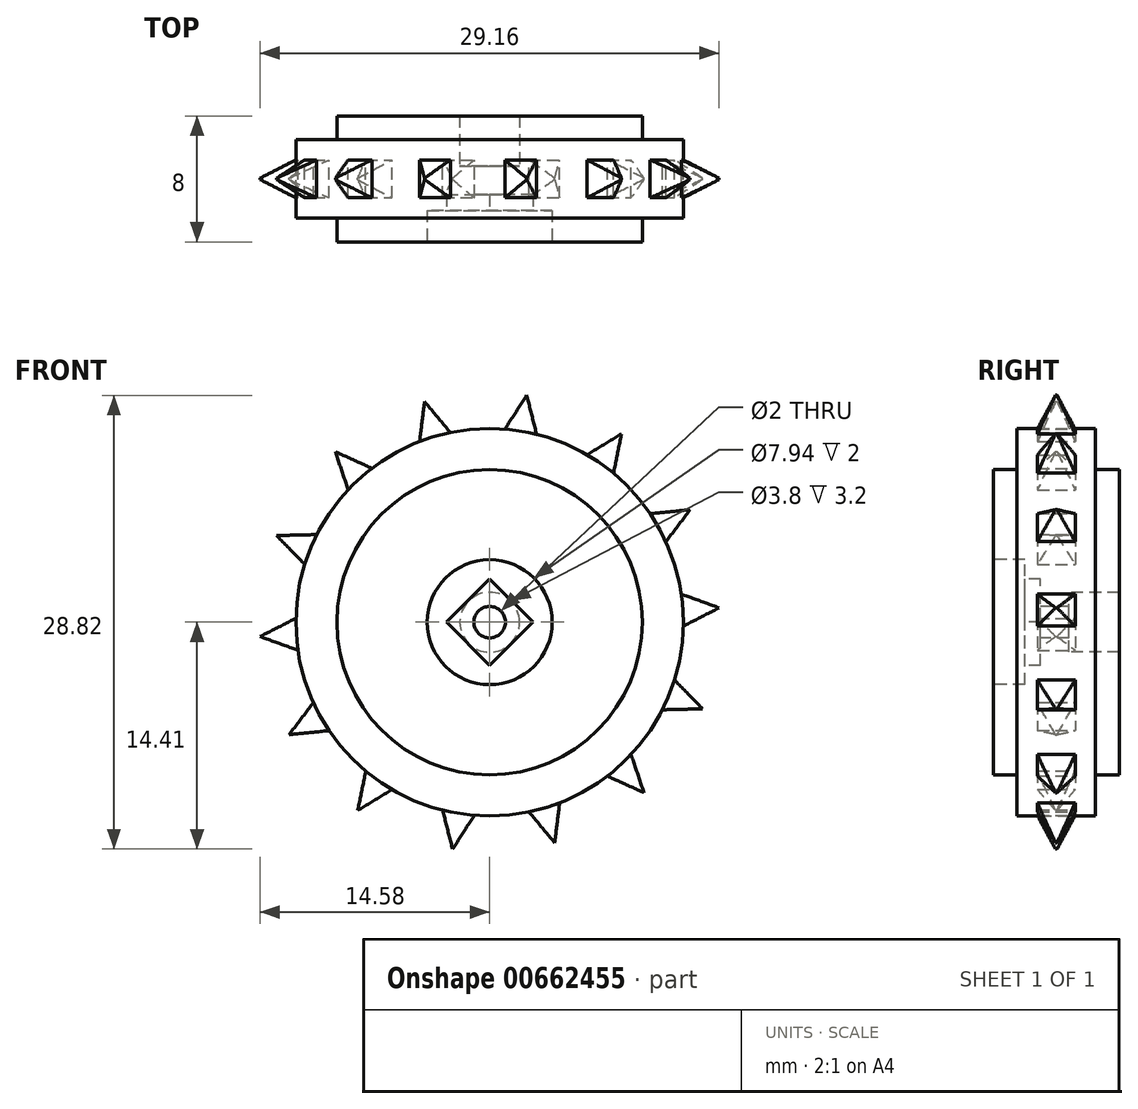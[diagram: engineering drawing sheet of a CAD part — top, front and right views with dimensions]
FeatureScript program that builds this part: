
annotation { "Feature Type Name" : "Feature", "Feature Type Description" : "" }
export const myFeature = defineFeature(function(context is Context, id is Id, definition is map)
    precondition{}
    {
        {
            var Q0;
            Q0=qCreatedBy(makeId("Front.planeOp"),FACE);
            var sketch = newSketch(context, id + "F0", { "sketchPlane" : qUnion([Q0])});
            skCircle(sketch, "E0.cCircle", {"center": v(-22.86, 35.79) * mm, "radius": 14.24 * mm, "construction": true});
            skLineSegment(sketch, "E0.0", {"start": v(-9.33, 30.29) * mm, "end": v(-13.06, 24.96) * mm});
            skLineSegment(sketch, "E0.1", {"start": v(-13.06, 24.96) * mm, "end": v(-18.73, 21.78) * mm});
            skLineSegment(sketch, "E0.2", {"start": v(-18.73, 21.78) * mm, "end": v(-25.21, 21.38) * mm});
            skLineSegment(sketch, "E0.3", {"start": v(-25.21, 21.38) * mm, "end": v(-31.24, 23.82) * mm});
            skLineSegment(sketch, "E0.4", {"start": v(-31.24, 23.82) * mm, "end": v(-35.6, 28.64) * mm});
            skLineSegment(sketch, "E0.5", {"start": v(-35.6, 28.64) * mm, "end": v(-37.44, 34.88) * mm});
            skLineSegment(sketch, "E0.6", {"start": v(-37.44, 34.88) * mm, "end": v(-36.39, 41.3) * mm});
            skLineSegment(sketch, "E0.7", {"start": v(-36.39, 41.3) * mm, "end": v(-32.66, 46.62) * mm});
            skLineSegment(sketch, "E0.8", {"start": v(-32.66, 46.62) * mm, "end": v(-27, 49.8) * mm});
            skLineSegment(sketch, "E0.9", {"start": v(-27, 49.8) * mm, "end": v(-20.5, 50.2) * mm});
            skLineSegment(sketch, "E0.10", {"start": v(-20.5, 50.2) * mm, "end": v(-14.48, 47.75) * mm});
            skLineSegment(sketch, "E0.11", {"start": v(-14.48, 47.75) * mm, "end": v(-10.12, 42.94) * mm});
            skLineSegment(sketch, "E0.12", {"start": v(-10.12, 42.94) * mm, "end": v(-8.28, 36.7) * mm});
            skLineSegment(sketch, "E0.13", {"start": v(-8.28, 36.7) * mm, "end": v(-9.33, 30.29) * mm});
            skPoint(sketch, "E0.0.midPoint", {"position": v(-11.2, 27.62) * mm});
            skLineSegment(sketch, "E1", {"start": v(-27, 49.8) * mm, "end": v(-22.86, 35.79) * mm});
            skLineSegment(sketch, "E2", {"start": v(-27, 49.8) * mm, "end": v(-27.37, 46.77) * mm});
            skLineSegment(sketch, "E3", {"start": v(-27.37, 46.77) * mm, "end": v(-26.2, 47.11) * mm, "construction": true});
            skLineSegment(sketch, "E4.MirrorCS", {"start": v(-27, 49.8) * mm, "end": v(-25.03, 47.46) * mm});
            skPoint(sketch, "E5", {"position": v(-26.34, 47.6) * mm});
            skPoint(sketch, "E6", {"position": v(-25.6, 45.1) * mm});
            skCircle(sketch, "E7", {"center": v(-22.86, 35.79) * mm, "radius": 9.7 * mm});
            skCircle(sketch, "E8", {"center": v(-22.86, 35.79) * mm, "radius": 12.3 * mm});
            skLineSegment(sketch, "E9.1.0", {"start": v(-32.66, 46.62) * mm, "end": v(-31.69, 43.72) * mm});
            skLineSegment(sketch, "E9.1.1", {"start": v(-32.66, 46.62) * mm, "end": v(-29.88, 45.36) * mm});
            skLineSegment(sketch, "E9.2.0", {"start": v(-36.39, 41.3) * mm, "end": v(-34.25, 39.1) * mm});
            skLineSegment(sketch, "E9.2.1", {"start": v(-36.39, 41.3) * mm, "end": v(-33.34, 41.37) * mm});
            skLineSegment(sketch, "E9.3.0", {"start": v(-37.44, 34.88) * mm, "end": v(-34.57, 33.84) * mm});
            skLineSegment(sketch, "E9.3.1", {"start": v(-37.44, 34.88) * mm, "end": v(-34.72, 36.27) * mm});
            skLineSegment(sketch, "E9.4.0", {"start": v(-35.6, 28.64) * mm, "end": v(-32.56, 28.95) * mm});
            skLineSegment(sketch, "E9.4.1", {"start": v(-35.6, 28.64) * mm, "end": v(-33.75, 31.08) * mm});
            skLineSegment(sketch, "E9.5.0", {"start": v(-31.24, 23.82) * mm, "end": v(-28.63, 25.42) * mm});
            skLineSegment(sketch, "E9.5.1", {"start": v(-31.24, 23.82) * mm, "end": v(-30.63, 26.82) * mm});
            skLineSegment(sketch, "E9.6.0", {"start": v(-25.21, 21.38) * mm, "end": v(-23.56, 23.94) * mm});
            skLineSegment(sketch, "E9.6.1", {"start": v(-25.21, 21.38) * mm, "end": v(-25.97, 24.34) * mm});
            skLineSegment(sketch, "E9.7.0", {"start": v(-18.73, 21.78) * mm, "end": v(-18.35, 24.81) * mm});
            skLineSegment(sketch, "E9.7.1", {"start": v(-18.73, 21.78) * mm, "end": v(-20.69, 24.12) * mm});
            skLineSegment(sketch, "E9.8.0", {"start": v(-13.06, 24.96) * mm, "end": v(-14.04, 27.85) * mm});
            skLineSegment(sketch, "E9.8.1", {"start": v(-13.06, 24.96) * mm, "end": v(-15.84, 26.22) * mm});
            skLineSegment(sketch, "E9.9.0", {"start": v(-9.33, 30.29) * mm, "end": v(-11.47, 32.47) * mm});
            skLineSegment(sketch, "E9.9.1", {"start": v(-9.33, 30.29) * mm, "end": v(-12.38, 30.21) * mm});
            skLineSegment(sketch, "E9.10.0", {"start": v(-8.28, 36.7) * mm, "end": v(-11.15, 37.74) * mm});
            skLineSegment(sketch, "E9.10.1", {"start": v(-8.28, 36.7) * mm, "end": v(-11, 35.31) * mm});
            skLineSegment(sketch, "E9.11.0", {"start": v(-10.12, 42.94) * mm, "end": v(-13.16, 42.63) * mm});
            skLineSegment(sketch, "E9.11.1", {"start": v(-10.12, 42.94) * mm, "end": v(-11.97, 40.5) * mm});
            skLineSegment(sketch, "E9.12.0", {"start": v(-14.48, 47.75) * mm, "end": v(-17.09, 46.16) * mm});
            skLineSegment(sketch, "E9.12.1", {"start": v(-14.48, 47.75) * mm, "end": v(-15.1, 44.76) * mm});
            skLineSegment(sketch, "E9.13.0", {"start": v(-20.5, 50.2) * mm, "end": v(-22.16, 47.64) * mm});
            skLineSegment(sketch, "E9.13.1", {"start": v(-20.5, 50.2) * mm, "end": v(-19.76, 47.24) * mm});
            skSolve(sketch);
        }
        {
            var Q0;
            Q0=makeQuery(id+"F0.imprint","IMPRINT",FACE,{"disambiguationData":[TD([[makeQuery(id+"F0.imprint","IMPRINT",EDGE,{"derivedFrom":sQuery(id+"F0.wireOp",EDGE,"E7")}),-1.0]])]});
            var Q1;
            {var subQ0=sQuery(id+"F0.wireOp",EDGE,"E9.2.1");var subQ1=sQuery(id+"F0.wireOp",EDGE,"E8");var subQ2=makeQuery(id+"F0.imprint","INTERSECT",VERTEX,{"derivedFrom":[subQ1,subQ0]});Q1=makeQuery(id+"F0.imprint","IMPRINT",FACE,{"disambiguationData":[TD([[makeQuery(id+"F0.imprint","IMPRINT",EDGE,{"disambiguationData":[TD([[subQ2,-1.0]])],"derivedFrom":subQ1}),-1.0]])]});}
            var Q2;
            {var subQ1=sQuery(id+"F0.wireOp",EDGE,"E2");var subQ3=sQuery(id+"F0.wireOp",EDGE,"E8");var subQ4=makeQuery(id+"F0.imprint","INTERSECT",VERTEX,{"derivedFrom":[subQ1,subQ3]});Q2=makeQuery(id+"F0.imprint","IMPRINT",FACE,{"disambiguationData":[TD([[makeQuery(id+"F0.imprint","IMPRINT",EDGE,{"disambiguationData":[TD([[subQ4,1.0]])],"derivedFrom":subQ3}),-1.0]])]});}
            var Q3;
            {var subQ0=sQuery(id+"F0.wireOp",EDGE,"E9.13.1");var subQ1=sQuery(id+"F0.wireOp",EDGE,"E8");var subQ2=makeQuery(id+"F0.imprint","INTERSECT",VERTEX,{"derivedFrom":[subQ1,subQ0]});Q3=makeQuery(id+"F0.imprint","IMPRINT",FACE,{"disambiguationData":[TD([[makeQuery(id+"F0.imprint","IMPRINT",EDGE,{"disambiguationData":[TD([[subQ2,-1.0]])],"derivedFrom":subQ1}),-1.0]])]});}
            var Q4;
            {var subQ0=sQuery(id+"F0.wireOp",EDGE,"E9.12.1");var subQ1=sQuery(id+"F0.wireOp",EDGE,"E8");var subQ2=makeQuery(id+"F0.imprint","INTERSECT",VERTEX,{"derivedFrom":[subQ1,subQ0]});Q4=makeQuery(id+"F0.imprint","IMPRINT",FACE,{"disambiguationData":[TD([[makeQuery(id+"F0.imprint","IMPRINT",EDGE,{"disambiguationData":[TD([[subQ2,-1.0]])],"derivedFrom":subQ1}),-1.0]])]});}
            var Q5;
            {var subQ0=sQuery(id+"F0.wireOp",EDGE,"E9.11.1");var subQ1=sQuery(id+"F0.wireOp",EDGE,"E8");var subQ2=makeQuery(id+"F0.imprint","INTERSECT",VERTEX,{"derivedFrom":[subQ1,subQ0]});Q5=makeQuery(id+"F0.imprint","IMPRINT",FACE,{"disambiguationData":[TD([[makeQuery(id+"F0.imprint","IMPRINT",EDGE,{"disambiguationData":[TD([[subQ2,-1.0]])],"derivedFrom":subQ1}),-1.0]])]});}
            var Q6;
            {var subQ0=sQuery(id+"F0.wireOp",EDGE,"E9.10.0");var subQ1=sQuery(id+"F0.wireOp",EDGE,"E8");var subQ2=makeQuery(id+"F0.imprint","INTERSECT",VERTEX,{"derivedFrom":[subQ1,subQ0]});Q6=makeQuery(id+"F0.imprint","IMPRINT",FACE,{"disambiguationData":[TD([[makeQuery(id+"F0.imprint","IMPRINT",EDGE,{"disambiguationData":[TD([[subQ2,1.0]])],"derivedFrom":subQ1}),-1.0]])]});}
            var Q7;
            {var subQ0=sQuery(id+"F0.wireOp",EDGE,"E9.9.1");var subQ1=sQuery(id+"F0.wireOp",EDGE,"E8");var subQ2=makeQuery(id+"F0.imprint","INTERSECT",VERTEX,{"derivedFrom":[subQ1,subQ0]});Q7=makeQuery(id+"F0.imprint","IMPRINT",FACE,{"disambiguationData":[TD([[makeQuery(id+"F0.imprint","IMPRINT",EDGE,{"disambiguationData":[TD([[subQ2,-1.0]])],"derivedFrom":subQ1}),-1.0]])]});}
            var Q8;
            {var subQ0=sQuery(id+"F0.wireOp",EDGE,"E9.8.1");var subQ1=sQuery(id+"F0.wireOp",EDGE,"E8");var subQ2=makeQuery(id+"F0.imprint","INTERSECT",VERTEX,{"derivedFrom":[subQ1,subQ0]});Q8=makeQuery(id+"F0.imprint","IMPRINT",FACE,{"disambiguationData":[TD([[makeQuery(id+"F0.imprint","IMPRINT",EDGE,{"disambiguationData":[TD([[subQ2,-1.0]])],"derivedFrom":subQ1}),-1.0]])]});}
            var Q9;
            {var subQ0=sQuery(id+"F0.wireOp",EDGE,"E9.7.1");var subQ1=sQuery(id+"F0.wireOp",EDGE,"E8");var subQ2=makeQuery(id+"F0.imprint","INTERSECT",VERTEX,{"derivedFrom":[subQ1,subQ0]});Q9=makeQuery(id+"F0.imprint","IMPRINT",FACE,{"disambiguationData":[TD([[makeQuery(id+"F0.imprint","IMPRINT",EDGE,{"disambiguationData":[TD([[subQ2,-1.0]])],"derivedFrom":subQ1}),-1.0]])]});}
            var Q10;
            {var subQ0=sQuery(id+"F0.wireOp",EDGE,"E9.6.1");var subQ1=sQuery(id+"F0.wireOp",EDGE,"E8");var subQ2=makeQuery(id+"F0.imprint","INTERSECT",VERTEX,{"derivedFrom":[subQ1,subQ0]});Q10=makeQuery(id+"F0.imprint","IMPRINT",FACE,{"disambiguationData":[TD([[makeQuery(id+"F0.imprint","IMPRINT",EDGE,{"disambiguationData":[TD([[subQ2,-1.0]])],"derivedFrom":subQ1}),-1.0]])]});}
            var Q11;
            {var subQ0=sQuery(id+"F0.wireOp",EDGE,"E9.5.1");var subQ1=sQuery(id+"F0.wireOp",EDGE,"E8");var subQ2=makeQuery(id+"F0.imprint","INTERSECT",VERTEX,{"derivedFrom":[subQ1,subQ0]});Q11=makeQuery(id+"F0.imprint","IMPRINT",FACE,{"disambiguationData":[TD([[makeQuery(id+"F0.imprint","IMPRINT",EDGE,{"disambiguationData":[TD([[subQ2,-1.0]])],"derivedFrom":subQ1}),-1.0]])]});}
            var Q12;
            {var subQ0=sQuery(id+"F0.wireOp",EDGE,"E9.4.1");var subQ1=sQuery(id+"F0.wireOp",EDGE,"E8");var subQ2=makeQuery(id+"F0.imprint","INTERSECT",VERTEX,{"derivedFrom":[subQ1,subQ0]});Q12=makeQuery(id+"F0.imprint","IMPRINT",FACE,{"disambiguationData":[TD([[makeQuery(id+"F0.imprint","IMPRINT",EDGE,{"disambiguationData":[TD([[subQ2,-1.0]])],"derivedFrom":subQ1}),-1.0]])]});}
            var Q13;
            {var subQ0=sQuery(id+"F0.wireOp",EDGE,"E9.3.1");var subQ1=sQuery(id+"F0.wireOp",EDGE,"E8");var subQ2=makeQuery(id+"F0.imprint","INTERSECT",VERTEX,{"derivedFrom":[subQ1,subQ0]});Q13=makeQuery(id+"F0.imprint","IMPRINT",FACE,{"disambiguationData":[TD([[makeQuery(id+"F0.imprint","IMPRINT",EDGE,{"disambiguationData":[TD([[subQ2,-1.0]])],"derivedFrom":subQ1}),-1.0]])]});}
            var Q14;
            Q14=makeQuery(id+"F0.imprint","IMPRINT",FACE,{"disambiguationData":[TD([[makeQuery(id+"F0.imprint","IMPRINT",EDGE,{"derivedFrom":sQuery(id+"F0.wireOp",EDGE,"E7")}),1.0]])]});
            var Q15;
            {var subQ0=sQuery(id+"F0.wireOp",EDGE,"E9.1.1");var subQ1=sQuery(id+"F0.wireOp",EDGE,"E8");var subQ2=makeQuery(id+"F0.imprint","INTERSECT",VERTEX,{"derivedFrom":[subQ1,subQ0]});Q15=makeQuery(id+"F0.imprint","IMPRINT",FACE,{"disambiguationData":[TD([[makeQuery(id+"F0.imprint","IMPRINT",EDGE,{"disambiguationData":[TD([[subQ2,-1.0]])],"derivedFrom":subQ1}),-1.0]])]});}
            var Q16;
            {var subQ1=sQuery(id+"F0.wireOp",EDGE,"E1");var subQ3=sQuery(id+"F0.wireOp",EDGE,"E8");var subQ4=makeQuery(id+"F0.imprint","INTERSECT",VERTEX,{"derivedFrom":[subQ1,subQ3]});Q16=makeQuery(id+"F0.imprint","IMPRINT",FACE,{"disambiguationData":[TD([[makeQuery(id+"F0.imprint","IMPRINT",EDGE,{"disambiguationData":[TD([[subQ4,1.0]])],"derivedFrom":subQ3}),-1.0]])]});}
            extrude(context, id + "F1", {"entities" : qUnion([Q0, Q1, Q2, Q3, Q4, Q5, Q6, Q7, Q8, Q9, Q10, Q11, Q12, Q13, Q14, Q15, Q16]), "endBound" : BoundingType.SYMMETRIC, "depth" : 2.4 * mm, "offsetDistance" : 25 * mm});
        }
        {
            var Q0;
            Q0=makeQuery(id+"F0.imprint","IMPRINT",FACE,{"disambiguationData":[TD([[makeQuery(id+"F0.imprint","IMPRINT",EDGE,{"derivedFrom":sQuery(id+"F0.wireOp",EDGE,"E7")}),-1.0]])]});
            var Q1;
            Q1=makeQuery(id+"F0.imprint","IMPRINT",FACE,{"disambiguationData":[TD([[makeQuery(id+"F0.imprint","IMPRINT",EDGE,{"derivedFrom":sQuery(id+"F0.wireOp",EDGE,"E7")}),1.0]])]});
            extrude(context, id + "F2", {"entities" : qUnion([Q0, Q1]), "operationType" : NewBodyOperationType.ADD, "endBound" : BoundingType.SYMMETRIC, "depth" : 5 * mm, "offsetDistance" : 25 * mm});
        }
        {
            var Q0;
            Q0=makeQuery(id+"F0.imprint","IMPRINT",FACE,{"disambiguationData":[TD([[makeQuery(id+"F0.imprint","IMPRINT",EDGE,{"derivedFrom":sQuery(id+"F0.wireOp",EDGE,"E7")}),1.0]])]});
            extrude(context, id + "F3", {"entities" : qUnion([Q0]), "operationType" : NewBodyOperationType.ADD, "endBound" : BoundingType.SYMMETRIC, "depth" : 8 * mm, "offsetDistance" : 25 * mm});
        }
        {
            var Q0;
            Q0=makeQuery(id+"F3.opExtrude","CAP_FACE",FACE,{"disambiguationData":[OSD([sQuery(id+"F0.wireOp",EDGE,"E7")])],"isStart":false});
            var sketch = newSketch(context, id + "F4", { "sketchPlane" : qUnion([Q0])});
            skPoint(sketch, "E10.0", {"position": v(-22.86, 35.79) * mm});
            skCircle(sketch, "E11.cCircle", {"center": v(-22.86, 35.79) * mm, "radius": 2.75 * mm, "construction": true});
            skLineSegment(sketch, "E11.0", {"start": v(-25.61, 35.79) * mm, "end": v(-22.86, 38.54) * mm});
            skLineSegment(sketch, "E11.1", {"start": v(-22.86, 38.54) * mm, "end": v(-20.1, 35.79) * mm});
            skLineSegment(sketch, "E11.2", {"start": v(-20.1, 35.79) * mm, "end": v(-22.86, 33.04) * mm});
            skLineSegment(sketch, "E11.3", {"start": v(-22.86, 33.04) * mm, "end": v(-25.61, 35.79) * mm});
            skCircle(sketch, "E12", {"center": v(-22.86, 35.79) * mm, "radius": 1 * mm});
            skCircle(sketch, "E13", {"center": v(-22.86, 35.79) * mm, "radius": 3.97 * mm});
            skCircle(sketch, "E14.0", {"center": v(-22.86, 35.79) * mm, "radius": 9.7 * mm});
            skSolve(sketch);
        }
        {
            var Q0;
            Q0=makeQuery(id+"F4.imprint","IMPRINT",FACE,{"disambiguationData":[TD([[makeQuery(id+"F4.imprint","IMPRINT",EDGE,{"derivedFrom":sQuery(id+"F4.wireOp",EDGE,"E12")}),1.0]])]});
            extrude(context, id + "F5", {"entities" : qUnion([Q0]), "operationType" : NewBodyOperationType.REMOVE, "endBound" : BoundingType.THROUGH_ALL, "oppositeDirection" : true, "depth" : 25 * mm, "offsetDistance" : 25 * mm});
        }
        {
            var Q0;
            Q0=makeQuery(id+"F4.imprint","IMPRINT",FACE,{"disambiguationData":[TD([[makeQuery(id+"F4.imprint","IMPRINT",EDGE,{"derivedFrom":sQuery(id+"F4.wireOp",EDGE,"E11.0")}),-1.0]])]});
            extrude(context, id + "F6", {"entities" : qUnion([Q0]), "operationType" : NewBodyOperationType.REMOVE, "oppositeDirection" : true, "depth" : 3 * mm, "offsetDistance" : 25 * mm});
        }
        {
            var Q0;
            Q0=makeQuery(id+"F4.imprint","IMPRINT",FACE,{"disambiguationData":[TD([[makeQuery(id+"F4.imprint","IMPRINT",EDGE,{"derivedFrom":sQuery(id+"F4.wireOp",EDGE,"E11.0")}),1.0]])]});
            extrude(context, id + "F7", {"entities" : qUnion([Q0]), "operationType" : NewBodyOperationType.REMOVE, "oppositeDirection" : true, "depth" : 2 * mm, "offsetDistance" : 25 * mm});
        }
        {
            var Q0;
            Q0=sQuery(id+"F0.wireOp",EDGE,"E1");
            extrude(context, id + "F8", {"bodyType" : ToolBodyType.SURFACE, "surfaceEntities" : qUnion([Q0]), "endBound" : BoundingType.SYMMETRIC, "depth" : 6 * mm, "offsetDistance" : 25 * mm});
        }
        {
            var Q0;
            Q0=makeQuery(id+"F8.opExtrude","SWEPT_FACE",FACE,{"disambiguationData":[OSD([sQuery(id+"F0.wireOp",EDGE,"E1")])]});
            var sketch = newSketch(context, id + "F9", { "sketchPlane" : qUnion([Q0])});
            skPoint(sketch, "E15.0", {"position": v(0, 55.4) * mm});
            skLineSegment(sketch, "E16.0", {"start": v(-1.2, 55.4) * mm, "end": v(-1.2, 53.06) * mm});
            skLineSegment(sketch, "E16.1", {"start": v(1.2, 55.4) * mm, "end": v(1.2, 53.06) * mm});
            skPoint(sketch, "E16.2", {"position": v(1.2, 53.1) * mm});
            skPoint(sketch, "E16.3", {"position": v(-1.2, 53.1) * mm});
            skLineSegment(sketch, "E17", {"start": v(-1.2, 53.1) * mm, "end": v(-0.04, 55.4) * mm});
            skLineSegment(sketch, "E18", {"start": v(-0.04, 55.4) * mm, "end": v(-1.2, 55.4) * mm});
            skLineSegment(sketch, "E19", {"start": v(0, 55.4) * mm, "end": v(0, 52.96) * mm, "construction": true});
            skLineSegment(sketch, "E20.MirrorCS", {"start": v(1.2, 53.1) * mm, "end": v(0.04, 55.4) * mm});
            skLineSegment(sketch, "E21.MirrorCS", {"start": v(0.04, 55.4) * mm, "end": v(1.2, 55.4) * mm});
            skSolve(sketch);
        }
        {
            var Q0;
            {var subQ2=sQuery(id+"F9.wireOp",EDGE,"E20.MirrorCS");Q0=makeQuery(id+"F9.imprint","IMPRINT",FACE,{"disambiguationData":[TD([[makeQuery(id+"F9.imprint","IMPRINT",EDGE,{"derivedFrom":subQ2}),-1.0]])]});}
            var Q1;
            {var subQ2=sQuery(id+"F9.wireOp",EDGE,"E17");Q1=makeQuery(id+"F9.imprint","IMPRINT",FACE,{"disambiguationData":[TD([[makeQuery(id+"F9.imprint","IMPRINT",EDGE,{"derivedFrom":subQ2}),1.0]])]});}
            var Q2;
            Q2=makeQuery(id+"F8.opExtrude","SWEPT_EDGE",EDGE,{"disambiguationData":[OSD([sQuery(id+"F0.wireOp",VERTEX,"E1.end")])]});
            revolve(context, id + "F10", {"operationType" : NewBodyOperationType.REMOVE, "entities" : qUnion([Q0, Q1]), "axis" : qUnion([Q2]), "revolveType" : RevolveType.FULL, "oppositeDirection" : true});
        }
        {
            var Q0;
            Q0=makeQuery(id+"F6.boolean.opBoolean","COPY",FACE,{"derivedFrom":makeQuery(id+"F6.opExtrude","CAP_FACE",FACE,{"disambiguationData":[OSD([sQuery(id+"F4.wireOp",EDGE,"E11.0"),sQuery(id+"F4.wireOp",EDGE,"E11.1"),sQuery(id+"F4.wireOp",EDGE,"E11.2"),sQuery(id+"F4.wireOp",EDGE,"E11.3"),sQuery(id+"F4.wireOp",EDGE,"E12")])],"isStart":false})});
            var sketch = newSketch(context, id + "F11", { "sketchPlane" : qUnion([Q0])});
            skCircle(sketch, "E22.0", {"center": v(-22.86, 35.79) * mm, "radius": 1 * mm});
            skCircle(sketch, "E23", {"center": v(-22.86, 35.79) * mm, "radius": 1.9 * mm});
            skSolve(sketch);
        }
        {
            var Q0;
            Q0=makeQuery(id+"F11.imprint","IMPRINT",FACE,{"disambiguationData":[TD([[makeQuery(id+"F11.imprint","IMPRINT",EDGE,{"derivedFrom":sQuery(id+"F11.wireOp",EDGE,"E22.0")}),-1.0]])]});
            extrude(context, id + "F12", {"entities" : qUnion([Q0]), "operationType" : NewBodyOperationType.REMOVE, "oppositeDirection" : true, "depth" : 7.6 * mm, "offsetDistance" : 25 * mm, "hasSecondDirection" : true, "secondDirectionOppositeDirection" : true, "secondDirectionDepth" : 1.8 * mm});
        }
    });
